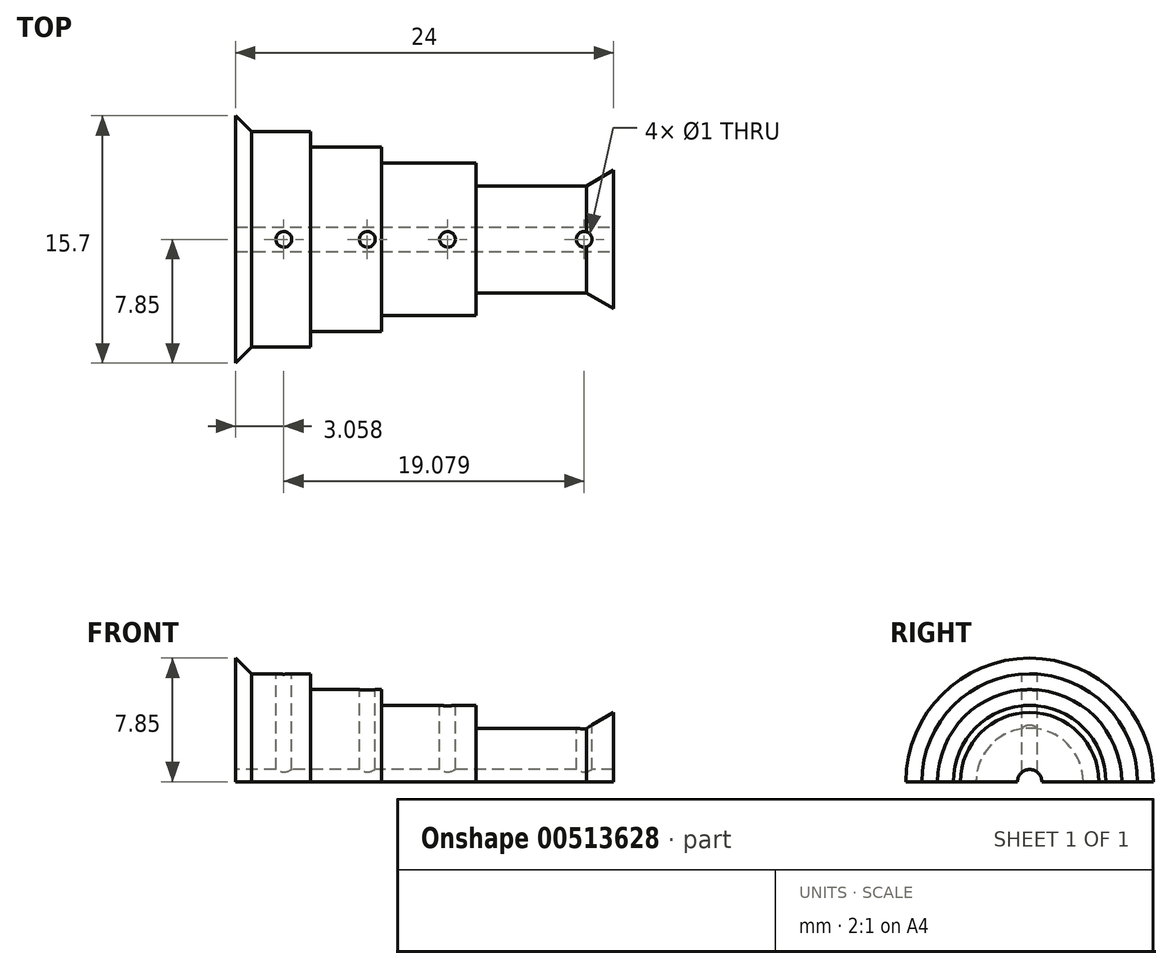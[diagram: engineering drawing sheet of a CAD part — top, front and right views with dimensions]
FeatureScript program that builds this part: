
annotation { "Feature Type Name" : "Feature", "Feature Type Description" : "" }
export const myFeature = defineFeature(function(context is Context, id is Id, definition is map)
    precondition{}
    {
        {
            var Q0;
            Q0=qCreatedBy(makeId("Front.planeOp"),FACE);
            var sketch = newSketch(context, id + "F0", { "sketchPlane" : qUnion([Q0])});
            skLineSegment(sketch, "E0", {"start": v(-22.67, 0) * mm, "end": v(34.76, 0) * mm, "construction": true});
            skLineSegment(sketch, "E1", {"start": v(0, 7.85) * mm, "end": v(0, 0) * mm});
            skLineSegment(sketch, "E2", {"start": v(0, 0) * mm, "end": v(0, 7.85) * mm});
            skLineSegment(sketch, "E3", {"start": v(24, 4.4) * mm, "end": v(24, 0) * mm});
            skLineSegment(sketch, "E4", {"start": v(0, 0.78) * mm, "end": v(24, 0.78) * mm});
            skLineSegment(sketch, "E5", {"start": v(22.27, 3.4) * mm, "end": v(24, 4.4) * mm});
            skLineSegment(sketch, "E6", {"start": v(24, 4.4) * mm, "end": v(24, 4.4) * mm});
            skLineSegment(sketch, "E7", {"start": v(1, 6.85) * mm, "end": v(4.77, 6.85) * mm});
            skLineSegment(sketch, "E8", {"start": v(15.27, 3.4) * mm, "end": v(22.27, 3.4) * mm});
            skLineSegment(sketch, "E9", {"start": v(1, 6.85) * mm, "end": v(0, 7.85) * mm});
            skLineSegment(sketch, "E10", {"start": v(4.77, 6.85) * mm, "end": v(4.77, 5.85) * mm});
            skLineSegment(sketch, "E11", {"start": v(4.77, 5.85) * mm, "end": v(9.27, 5.85) * mm});
            skLineSegment(sketch, "E12", {"start": v(9.27, 5.85) * mm, "end": v(9.27, 4.85) * mm});
            skLineSegment(sketch, "E13", {"start": v(9.27, 4.85) * mm, "end": v(15.27, 4.85) * mm});
            skLineSegment(sketch, "E14", {"start": v(15.27, 4.85) * mm, "end": v(15.27, 3.4) * mm});
            skSolve(sketch);
        }
        {
            var Q0;
            Q0=qSketchRegion(id+"F0",true);
            var Q1;
            Q1=sQuery(id+"F0.wireOp",EDGE,"E0");
            revolve(context, id + "F1", {"entities" : qUnion([Q0]), "axis" : qUnion([Q1]), "revolveType" : RevolveType.TWO_DIRECTIONS, "angle" : 90 * degree, "angleBack" : 270 * degree});
        }
        {
            var Q0;
            Q0=qCreatedBy(makeId("Top.planeOp"),FACE);
            var sketch = newSketch(context, id + "F2", { "sketchPlane" : qUnion([Q0])});
            skCircle(sketch, "E15", {"center": v(3.06, 0) * mm, "radius": 0.5 * mm});
            skCircle(sketch, "E16", {"center": v(8.36, 0) * mm, "radius": 0.5 * mm});
            skCircle(sketch, "E17", {"center": v(13.46, 0) * mm, "radius": 0.5 * mm});
            skCircle(sketch, "E18", {"center": v(22.14, 0) * mm, "radius": 0.5 * mm});
            skSolve(sketch);
        }
        {
            var Q0;
            Q0=qSketchRegion(id+"F2",true);
            extrude(context, id + "F3", {"entities" : qUnion([Q0]), "operationType" : NewBodyOperationType.REMOVE, "endBound" : BoundingType.SYMMETRIC, "oppositeDirection" : true, "depth" : 25 * mm, "offsetDistance" : 25 * mm});
        }
    });
